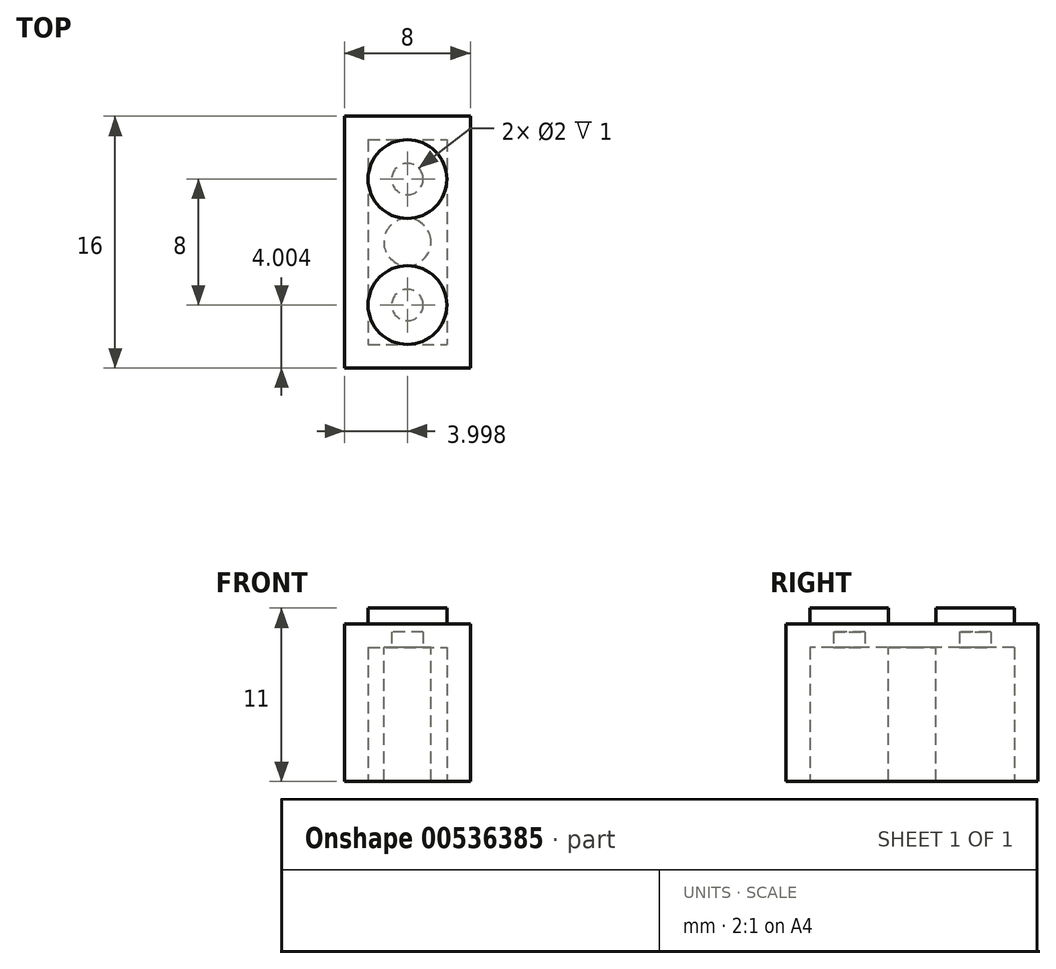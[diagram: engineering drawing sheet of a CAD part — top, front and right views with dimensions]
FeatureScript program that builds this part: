
annotation { "Feature Type Name" : "Feature", "Feature Type Description" : "" }
export const myFeature = defineFeature(function(context is Context, id is Id, definition is map)
    precondition{}
    {
        {
            var Q0;
            Q0=qCreatedBy(makeId("Top.planeOp"),FACE);
            var sketch = newSketch(context, id + "F0", { "sketchPlane" : qUnion([Q0])});
            skLineSegment(sketch, "E0.bottom", {"start": v(-10.52, 19.44) * mm, "end": v(-2.52, 19.44) * mm});
            skLineSegment(sketch, "E0.top", {"start": v(-10.52, 3.44) * mm, "end": v(-2.52, 3.44) * mm});
            skLineSegment(sketch, "E0.left", {"start": v(-10.52, 19.44) * mm, "end": v(-10.52, 3.44) * mm});
            skLineSegment(sketch, "E0.right", {"start": v(-2.52, 19.44) * mm, "end": v(-2.52, 3.44) * mm});
            skSolve(sketch);
        }
        {
            var Q0;
            Q0=makeQuery(id+"F0.imprint","IMPRINT",FACE,{"disambiguationData":[TD([[makeQuery(id+"F0.imprint","IMPRINT",EDGE,{"derivedFrom":sQuery(id+"F0.wireOp",EDGE,"E0.bottom")}),-1.0]])]});
            extrude(context, id + "F1", {"entities" : qUnion([Q0]), "depth" : 10 * mm, "offsetDistance" : 25 * mm});
        }
        {
            var Q0;
            Q0=makeQuery(id+"F1.opExtrude","CAP_FACE",FACE,{"disambiguationData":[OSD([sQuery(id+"F0.wireOp",EDGE,"E0.bottom"),sQuery(id+"F0.wireOp",EDGE,"E0.top"),sQuery(id+"F0.wireOp",EDGE,"E0.left"),sQuery(id+"F0.wireOp",EDGE,"E0.right")])],"isStart":false});
            var sketch = newSketch(context, id + "F2", { "sketchPlane" : qUnion([Q0])});
            skCircle(sketch, "E1", {"center": v(-6.52, 7.44) * mm, "radius": 2.5 * mm});
            skPoint(sketch, "E1.centerSnap0", {"position": v(-6.52, 3.44) * mm});
            skCircle(sketch, "E2", {"center": v(-6.52, 15.44) * mm, "radius": 2.5 * mm});
            skPoint(sketch, "E2.centerSnap0", {"position": v(-6.52, 19.44) * mm});
            skSolve(sketch);
        }
        {
            var Q0;
            Q0=makeQuery(id+"F2.imprint","IMPRINT",FACE,{"disambiguationData":[TD([[makeQuery(id+"F2.imprint","IMPRINT",EDGE,{"derivedFrom":sQuery(id+"F2.wireOp",EDGE,"E1")}),1.0]])]});
            var Q1;
            Q1=makeQuery(id+"F2.imprint","IMPRINT",FACE,{"disambiguationData":[TD([[makeQuery(id+"F2.imprint","IMPRINT",EDGE,{"derivedFrom":sQuery(id+"F2.wireOp",EDGE,"E2")}),1.0]])]});
            extrude(context, id + "F3", {"entities" : qUnion([Q0, Q1]), "operationType" : NewBodyOperationType.ADD, "depth" : 1 * mm, "offsetDistance" : 25 * mm});
        }
        {
            var Q0;
            Q0=makeQuery(id+"F1.opExtrude","CAP_FACE",FACE,{"disambiguationData":[OSD([sQuery(id+"F0.wireOp",EDGE,"E0.bottom"),sQuery(id+"F0.wireOp",EDGE,"E0.top"),sQuery(id+"F0.wireOp",EDGE,"E0.left"),sQuery(id+"F0.wireOp",EDGE,"E0.right")])],"isStart":true});
            shell(context, id + "F4", {"entities" : qUnion([Q0]), "thickness" : 1.5 * mm});
        }
        {
            var Q0;
            Q0=makeQuery(id+"F1.opExtrude","CAP_FACE",FACE,{"disambiguationData":[OSD([sQuery(id+"F0.wireOp",EDGE,"E0.bottom"),sQuery(id+"F0.wireOp",EDGE,"E0.top"),sQuery(id+"F0.wireOp",EDGE,"E0.left"),sQuery(id+"F0.wireOp",EDGE,"E0.right")])],"isStart":false});
            var sketch = newSketch(context, id + "F5", { "sketchPlane" : qUnion([Q0])});
            skCircle(sketch, "E3", {"center": v(-6.52, 11.44) * mm, "radius": 1.5 * mm});
            skPoint(sketch, "E3.centerSnap0", {"position": v(-6.52, 3.44) * mm});
            skPoint(sketch, "E3.centerSnap1", {"position": v(-10.52, 11.44) * mm});
            skSolve(sketch);
        }
        {
            var Q0;
            {var subQ0=sQuery(id+"F5.wireOp",EDGE,"E3");var subQ1=makeQuery(id+"F5.imprint","INTERSECT",VERTEX,{"derivedFrom":[makeQuery(id+"F3.opExtrude","CAP_EDGE",EDGE,{"disambiguationData":[OSD([sQuery(id+"F2.wireOp",EDGE,"E1")])],"isStart":true}),subQ0]});Q0=makeQuery(id+"F5.imprint","IMPRINT",FACE,{"disambiguationData":[TD([[makeQuery(id+"F5.imprint","IMPRINT",EDGE,{"disambiguationData":[TD([[subQ1,1.0]])],"derivedFrom":subQ0}),1.0]])]});}
            var Q1;
            Q1=sQuery(id+"F5.wireOp",EDGE,"E3");
            extrude(context, id + "F6", {"entities" : qUnion([Q0]), "operationType" : NewBodyOperationType.ADD, "surfaceEntities" : qUnion([Q1]), "oppositeDirection" : true, "depth" : 10 * mm, "offsetDistance" : 25 * mm});
        }
    });
